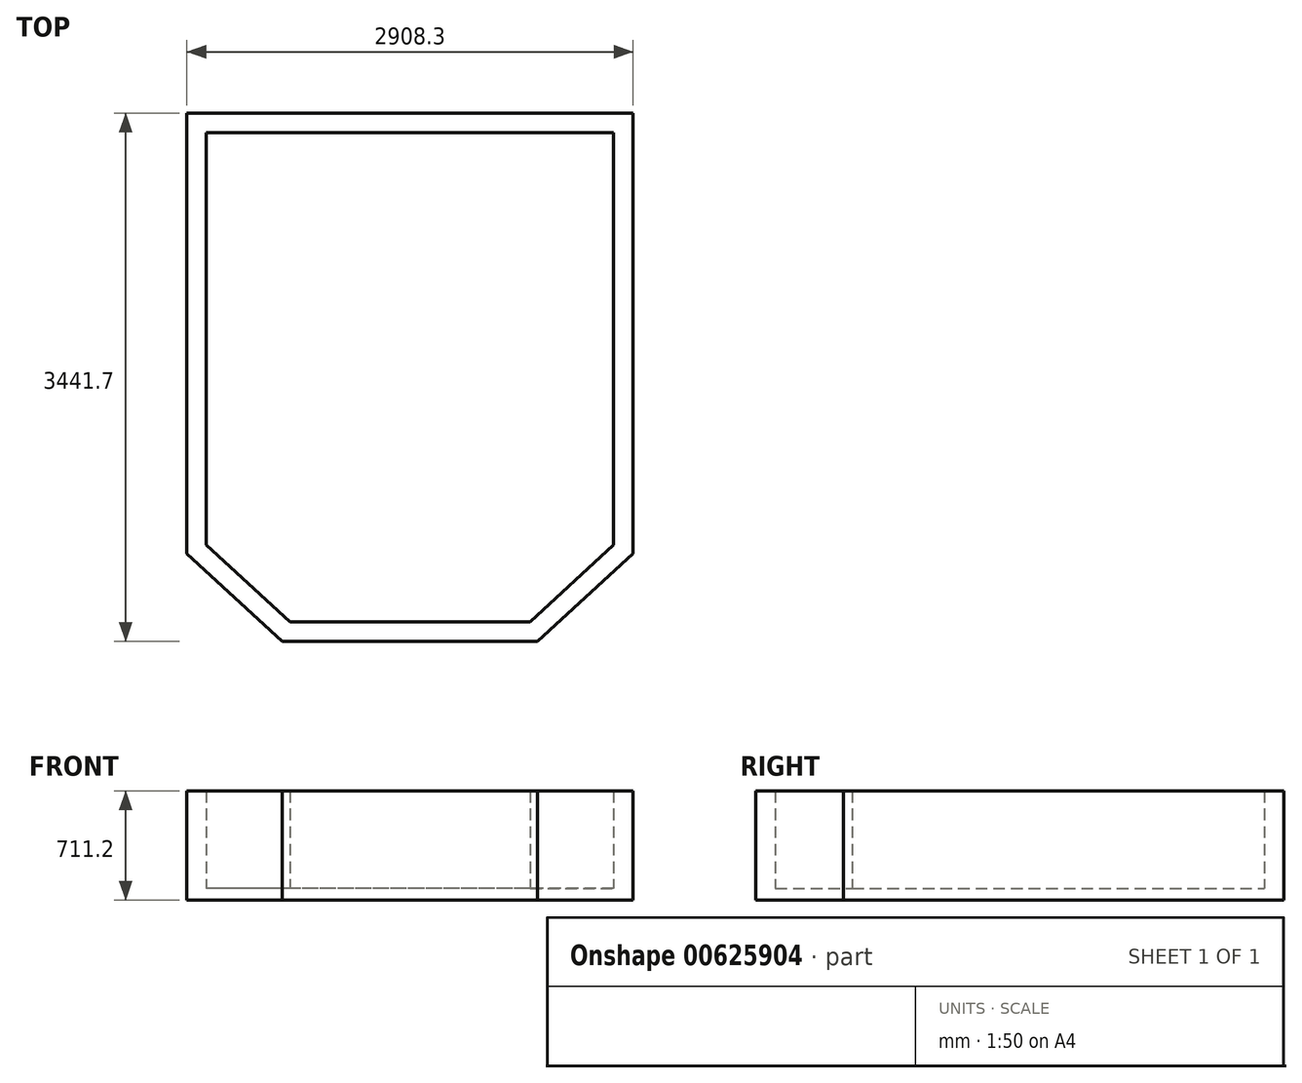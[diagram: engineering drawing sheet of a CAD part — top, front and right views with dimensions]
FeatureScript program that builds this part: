
annotation { "Feature Type Name" : "Feature", "Feature Type Description" : "" }
export const myFeature = defineFeature(function(context is Context, id is Id, definition is map)
    precondition{}
    {
        {
            var Q0;
            Q0=qCreatedBy(makeId("Top.planeOp"),FACE);
            var sketch = newSketch(context, id + "F0", { "sketchPlane" : qUnion([Q0])});
            skLineSegment(sketch, "E0", {"start": v(0, 0) * mm, "end": v(2908.3, 0) * mm});
            skLineSegment(sketch, "E1", {"start": v(2908.3, 0) * mm, "end": v(2908.3, -2870.2) * mm});
            skLineSegment(sketch, "E2", {"start": v(2908.3, -2870.2) * mm, "end": v(2286, -3441.7) * mm});
            skLineSegment(sketch, "E3", {"start": v(0, 0) * mm, "end": v(0, -2870.2) * mm});
            skLineSegment(sketch, "E4", {"start": v(0, -2870.2) * mm, "end": v(622.3, -3441.7) * mm});
            skLineSegment(sketch, "E5", {"start": v(622.3, -3441.7) * mm, "end": v(2286, -3441.7) * mm});
            skSolve(sketch);
        }
        {
            var Q0;
            Q0 = qSketchRegion(id + "F0", true);
            extrude(context, id + "F1", {"entities" : qUnion([Q0]), "oppositeDirection" : true, "depth" : 76.2 * mm, "offsetDistance" : 25.4 * mm});
        }
        {
            var Q0;
            Q0=makeQuery(id+"F1.opExtrude","CAP_FACE",FACE,{"disambiguationData":[OSD([sQuery(id+"F0.wireOp",EDGE,"E0"),sQuery(id+"F0.wireOp",EDGE,"E1"),sQuery(id+"F0.wireOp",EDGE,"E2"),sQuery(id+"F0.wireOp",EDGE,"E3"),sQuery(id+"F0.wireOp",EDGE,"E4"),sQuery(id+"F0.wireOp",EDGE,"E5")])],"isStart":true});
            var sketch = newSketch(context, id + "F2", { "sketchPlane" : qUnion([Q0])});
            skLineSegment(sketch, "E6.0", {"start": v(127, -2814.4) * mm, "end": v(127, -127) * mm});
            skLineSegment(sketch, "E6.1", {"start": v(2781.3, -2814.4) * mm, "end": v(2781.3, -127) * mm});
            skLineSegment(sketch, "E6.2", {"start": v(2236.53, -3314.7) * mm, "end": v(2781.3, -2814.4) * mm});
            skLineSegment(sketch, "E6.3", {"start": v(2781.3, -127) * mm, "end": v(127, -127) * mm});
            skLineSegment(sketch, "E6.4", {"start": v(2236.53, -3314.7) * mm, "end": v(671.77, -3314.7) * mm});
            skLineSegment(sketch, "E6.5", {"start": v(671.77, -3314.7) * mm, "end": v(127, -2814.4) * mm});
            skSolve(sketch);
        }
        {
            var Q0;
            Q0=makeQuery(id+"F2.imprint","IMPRINT",FACE,{"disambiguationData":[TD([[makeQuery(id+"F2.imprint","IMPRINT",EDGE,{"derivedFrom":sQuery(id+"F2.wireOp",EDGE,"E6.0")}),1.0]])]});
            extrude(context, id + "F3", {"entities" : qUnion([Q0]), "operationType" : NewBodyOperationType.ADD, "depth" : 635 * mm, "offsetDistance" : 25.4 * mm});
        }
    });
